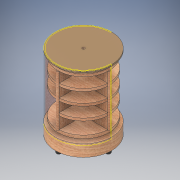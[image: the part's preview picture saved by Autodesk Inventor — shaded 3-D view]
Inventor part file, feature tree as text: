
AUTODESK INVENTOR PART (.ipt)
format: ipt  version: 2017 (Build 210142000, 142)  size: 697,856 bytes
history: native  units: in
note: dims shown in document units (in); Inventor stores cm internally (conversion verified against a paired STEP export)
features: sketch x47, extrude x36, plane x7, other x7, move_body x6, fillet x4, thread x1, pattern_circular x1
ambient origin geometry x8: Origin, YZ Plane, XZ Plane, XY Plane, X Axis, Y Axis, Z Axis, Center Point
bodies: Solid1 (feature_tree), Solid2 (feature_tree), Solid3 (feature_tree)
feature tree (109):
  sketch  "3D Sketch1"
  extrude  "Extrusion1"  Depth=0.5in
  sketch  "3D Sketch2"
  extrude  "Extrusion2"  Depth=10.0in
  extrude  "Extrusion3"  Depth=11.25in TaperAngle=0.0deg
  extrude  "Extrusion4"  Depth=0.5in TaperAngle=0.0deg
  thread  "Thread1"  [1 undecoded]
  extrude  "Extrusion5"  Depth=13.0in TaperAngle=0.0deg
  extrude  "Extrusion6"  Depth=2.6875in TaperAngle=0.0deg
  sketch  "Sketch7"  dims[d26=2.5in d27=0.0in d28=2.0in d29=0.0in]
  extrude  "Extrusion7"  Depth=2.0in TaperAngle=0.0deg
  extrude  "Extrusion9"  Depth=2.0in TaperAngle=0.0deg
  sketch  "Sketch13"  dims[d42=3.0in d43=0.0in d44=2.5in d45=0.0in]
  sketch  "Sketch14"  dims[d46=0.0in d47=3.0in d48=0.0in d49=0.5in d50=0.0in]
  sketch  "Sketch15"  dims[d51=0.0in d52=2.5in d53=0.0in d55=0.5in d56=0.0in]
  extrude  "Extrusion10"  Depth=2.0in TaperAngle=0.0deg
  extrude  "Extrusion11"  Depth=2.5in TaperAngle=0.0deg
  sketch  "Sketch17"  dims[d60=2.5in d61=0.0in d62=0.0in d63=2.5in d64=0.0in]
  extrude  "Extrusion12"  Depth=0.5in TaperAngle=0.0deg
  extrude  "Extrusion13"  Depth=0.5in TaperAngle=0.0deg
  sketch  "Sketch19"  dims[d70=0.5in d71=0.0in d72=5.5in d73=0.0in]
  sketch  "Sketch20"  dims[d74=5.0in d75=0.0in d76=0.0in d77=2.5in d78=0.0in]
  extrude  "Extrusion16"  Depth=3.0in TaperAngle=0.0deg
  extrude  "Extrusion17"  Depth=2.5in TaperAngle=0.0deg
  sketch  "Sketch22"  dims[d79=0.5in d80=0.0in d85=0.0in d86=-1.5in d87=0.0in]
  extrude  "Extrusion18"  Depth=2.5in TaperAngle=0.0deg
  extrude  "Extrusion19"  Depth=5.5in TaperAngle=0.0deg
  sketch  "Sketch25"  dims[d90=0.5in d91=0.0in d92=0.2in]
  move_body  "Move Body1"
  plane  "Work Plane3"
  extrude  "Extrusion20"  Depth=2.5in TaperAngle=0.0deg
  move_body  "Move Body2"
  plane  "Work Plane2"
  extrude  "Extrusion21"  TaperAngle=0.0deg  [1 undecoded]
  sketch  "Sketch29"  dims[d98=11.0in d99=0.3in d100=0.0in]
  sketch  "Sketch30"  dims[d101=11.0in d102=0.3in d103=0.0in]
  extrude  "Extrusion22"  Depth=1.0in
  extrude  "Extrusion23"  Depth=0.2in
  plane  "Work Plane8"
  sketch  "Sketch32"  dims[d116=0.2in d117=11.0in d118=2.0in d119=0.0in d133=1.5748in d134=360.0deg d136=2.0in d138=2.0in]
  move_body  "Move Body3"
  plane  "Work Plane11"
  extrude  "Extrusion24"  Depth=0.5in
  move_body  "Move Body4"
  plane  "Work Plane6"
  extrude  "Extrusion25"  Depth=1.0in TaperAngle=0.0deg
  sketch  "Sketch35"  dims[d145=2.0in d146=0.5in d147=0.0in]
  sketch  "Sketch36"  dims[d148=0.1in d149=0.0in]
  extrude  "Extrusion26"  Depth=0.3in TaperAngle=0.0deg
  extrude  "Extrusion27"  Depth=0.3in TaperAngle=0.0deg
  move_body  "Move Body5"
  plane  "Work Plane9"
  extrude  "Extrusion28"  Depth=0.2in
  sketch  "Sketch40"  dims[d152=0.911in]
  move_body  "Move Body6"
  plane  "Work Plane12"
  extrude  "Extrusion29"  Depth=11.0in
  fillet  "Fillet1"  Radius=2.0in
  fillet  "Fillet2"  Radius=1.5748in
  fillet  "Fillet3"  Radius=2.0in
  fillet  "Fillet4"  Radius=2.0in
  sketch  "Sketch42"  dims[d154=0.911in d155=0.45in]
  extrude  "Extrusion30"  Depth=8.0in TaperAngle=0.0deg
  extrude  "Extrusion31"  Depth=0.3in TaperAngle=0.0deg
  extrude  "Extrusion34"  Depth=0.5in TaperAngle=0.0deg
  sketch  "Sketch49"  dims[d164=0.911in d165=0.45in]
  other  "Form1"
  pattern_circular  "Circular Pattern2"  [2 undecoded]
  extrude  "Extrusion36"  [1 undecoded]
  extrude  "Extrusion37"  [1 undecoded]
  other  "Form2"
  extrude  "Extrusion38"  [1 undecoded]
  extrude  "Extrusion39"  [1 undecoded]
  extrude  "Extrusion40"  [1 undecoded]
  extrude  "Extrusion41"  [1 undecoded]
  sketch  "Sketch1"  dims[d2=0.5in d3=0.5in]
  sketch  "Sketch2"  dims[d4=10.0in d5=0.0in d6=10.0in]
  sketch  "Sketch3"  dims[d7=0.5in d8=0.0in d9=11.25in d10=0.0in]
  sketch  "Sketch4"  dims[d11=1.8in d12=0.5in d13=0.0in d14=1.0in d15=0.0in]
  sketch  "Sketch5"  dims[d16=0.5in d17=0.0in d18=13.0in d19=0.0in]
  sketch  "Sketch6"  dims[d20=2.8in d21=0.0in d24=2.6875in d25=0.0in]
  sketch  "Sketch8"  dims[d30=2.5in d31=0.0in d32=2.0in d33=0.0in]
  sketch  "Sketch12"  dims[d38=2.5in d39=0.0in d40=2.0in d41=0.0in]
  sketch  "Sketch16"  dims[d57=0.5in d58=3.0in d59=0.0in]
  sketch  "Sketch18"  dims[d65=0.5in d66=0.0in d67=0.0in d68=2.5in d69=0.0in]
  sketch  "Sketch24"  dims[d88=1.0in d89=1.0in]
  sketch  "Sketch26"  dims[d93=0.2in d94=0.5in]
  sketch  "Sketch28"  dims[d95=0.5in d96=1.0in d97=0.0in]
  sketch  "Sketch31"  dims[d105=12.6125in d106=0.0in d115=0.2in]
  sketch  "Sketch33"  dims[d139=0.7in d140=8.0in d141=0.0in]
  sketch  "Sketch34"  dims[d142=2.0in d143=0.3in d144=0.0in]
  sketch  "Sketch37"  dims[d150=0.3in d151=0.0in]
  sketch  "Sketch41"  dims[d153=0.45in]
  sketch  "Sketch43"  dims[d156=0.911in d157=0.45in]
  sketch  "Sketch44"  dims[d158=0.911in d159=0.45in]
  sketch  "Sketch45"  dims[d160=0.911in d161=0.45in]
  other  "Srf5"
  sketch  "Sketch48"  dims[d162=0.911in d163=0.45in]
  sketch  "Sketch51"  dims[d166=0.911in d167=0.45in]
  sketch  "Sketch52"  dims[d168=0.1in d169=0.0in]
  sketch  "Sketch53"
  sketch  "Sketch54"
  sketch  "Sketch55"
  sketch  "Sketch56"
  extrude  "ExtrusionSrf1"  [1 undecoded]
  other  "Srf1"
  other  "Srf2"
  other  "Srf3"
  other  "Srf4"
note: 11 required parameter values undecoded (feature->parameter linkage not recoverable at this tier; creation-order binding heuristic only, values carry confidence <= 0.55)
